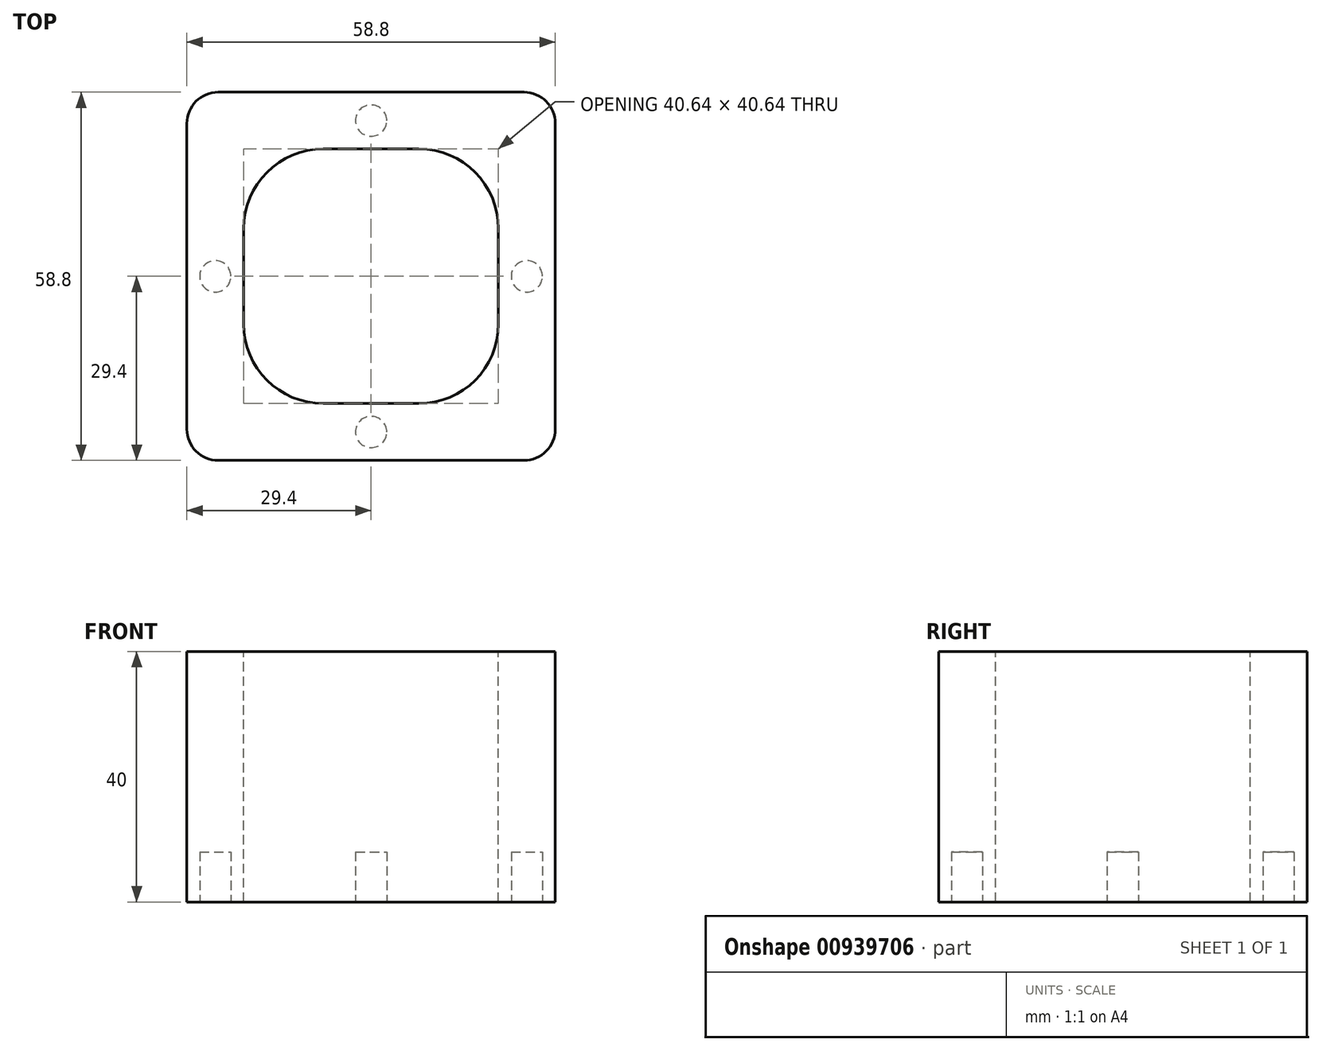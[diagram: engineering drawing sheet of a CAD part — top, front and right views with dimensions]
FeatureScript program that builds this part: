
annotation { "Feature Type Name" : "Feature", "Feature Type Description" : "" }
export const myFeature = defineFeature(function(context is Context, id is Id, definition is map)
    precondition{}
    {
        {
            var Q0;
            Q0=qCreatedBy(makeId("Top.planeOp"),FACE);
            var sketch = newSketch(context, id + "F0", { "sketchPlane" : qUnion([Q0])});
            skLineSegment(sketch, "E0.bottom", {"start": v(29.4, -29.4) * mm, "end": v(-29.4, -29.4) * mm});
            skLineSegment(sketch, "E0.top", {"start": v(29.4, 29.4) * mm, "end": v(-29.4, 29.4) * mm});
            skLineSegment(sketch, "E0.left", {"start": v(29.4, -29.4) * mm, "end": v(29.4, 29.4) * mm});
            skLineSegment(sketch, "E0.right", {"start": v(-29.4, -29.4) * mm, "end": v(-29.4, 29.4) * mm});
            skPoint(sketch, "E0.middle", {"position": v(0, 0) * mm});
            skSolve(sketch);
        }
        {
            var Q0;
            Q0=makeQuery(id+"F0.imprint","IMPRINT",FACE,{"disambiguationData":[TD([[makeQuery(id+"F0.imprint","IMPRINT",EDGE,{"derivedFrom":sQuery(id+"F0.wireOp",EDGE,"E0.bottom")}),-1.0]])]});
            extrude(context, id + "F1", {"entities" : qUnion([Q0]), "depth" : 40 * mm, "offsetDistance" : 25 * mm});
        }
        {
            var Q0;
            Q0=makeQuery(id+"F1.opExtrude","CAP_FACE",FACE,{"disambiguationData":[OSD([sQuery(id+"F0.wireOp",EDGE,"E0.bottom"),sQuery(id+"F0.wireOp",EDGE,"E0.top"),sQuery(id+"F0.wireOp",EDGE,"E0.left"),sQuery(id+"F0.wireOp",EDGE,"E0.right")])],"isStart":false});
            var sketch = newSketch(context, id + "F2", { "sketchPlane" : qUnion([Q0])});
            skLineSegment(sketch, "E1.bottom", {"start": v(20.32, -20.32) * mm, "end": v(-20.32, -20.32) * mm});
            skLineSegment(sketch, "E1.top", {"start": v(20.32, 20.32) * mm, "end": v(-20.32, 20.32) * mm});
            skLineSegment(sketch, "E1.left", {"start": v(20.32, -20.32) * mm, "end": v(20.32, 20.32) * mm});
            skLineSegment(sketch, "E1.right", {"start": v(-20.32, -20.32) * mm, "end": v(-20.32, 20.32) * mm});
            skPoint(sketch, "E1.middle", {"position": v(0, 0) * mm});
            skSolve(sketch);
        }
        {
            var Q0;
            Q0=makeQuery(id+"F2.imprint","IMPRINT",FACE,{"disambiguationData":[TD([[makeQuery(id+"F2.imprint","IMPRINT",EDGE,{"derivedFrom":sQuery(id+"F2.wireOp",EDGE,"E1.bottom")}),-1.0]])]});
            extrude(context, id + "F3", {"entities" : qUnion([Q0]), "operationType" : NewBodyOperationType.REMOVE, "endBound" : BoundingType.THROUGH_ALL, "oppositeDirection" : true, "depth" : 25 * mm, "offsetDistance" : 25 * mm});
        }
        {
            var Q0;
            Q0=makeQuery(id+"F1.opExtrude","CAP_FACE",FACE,{"disambiguationData":[OSD([sQuery(id+"F0.wireOp",EDGE,"E0.bottom"),sQuery(id+"F0.wireOp",EDGE,"E0.top"),sQuery(id+"F0.wireOp",EDGE,"E0.left"),sQuery(id+"F0.wireOp",EDGE,"E0.right")])],"isStart":true});
            var sketch = newSketch(context, id + "F4", { "sketchPlane" : qUnion([Q0])});
            skCircle(sketch, "E2", {"center": v(-24.86, 0) * mm, "radius": 2.5 * mm});
            skCircle(sketch, "E3", {"center": v(0, 24.86) * mm, "radius": 2.5 * mm});
            skCircle(sketch, "E4", {"center": v(24.86, 0) * mm, "radius": 2.5 * mm});
            skCircle(sketch, "E5", {"center": v(0, -24.86) * mm, "radius": 2.5 * mm});
            skSolve(sketch);
        }
        {
            var Q0;
            Q0 = qSketchRegion(id + "F4", true);
            extrude(context, id + "F5", {"entities" : qUnion([Q0]), "operationType" : NewBodyOperationType.REMOVE, "oppositeDirection" : true, "depth" : 8 * mm, "offsetDistance" : 25 * mm});
        }
        {
            var Q0;
            Q0=makeQuery(id+"F3.boolean.opBoolean","COPY",EDGE,{"derivedFrom":makeQuery(id+"F3.opExtrude","SWEPT_EDGE",EDGE,{"disambiguationData":[OSD([sQuery(id+"F2.wireOp",EDGE,"E1.top"),sQuery(id+"F2.wireOp",EDGE,"E1.right")])]})});
            var Q1;
            Q1=makeQuery(id+"F3.boolean.opBoolean","COPY",EDGE,{"derivedFrom":makeQuery(id+"F3.opExtrude","SWEPT_EDGE",EDGE,{"disambiguationData":[OSD([sQuery(id+"F2.wireOp",EDGE,"E1.top"),sQuery(id+"F2.wireOp",EDGE,"E1.left")])]})});
            var Q2;
            Q2=makeQuery(id+"F3.boolean.opBoolean","COPY",EDGE,{"derivedFrom":makeQuery(id+"F3.opExtrude","SWEPT_EDGE",EDGE,{"disambiguationData":[OSD([sQuery(id+"F2.wireOp",EDGE,"E1.bottom"),sQuery(id+"F2.wireOp",EDGE,"E1.left")])]})});
            var Q3;
            Q3=makeQuery(id+"F3.boolean.opBoolean","COPY",EDGE,{"derivedFrom":makeQuery(id+"F3.opExtrude","SWEPT_EDGE",EDGE,{"disambiguationData":[OSD([sQuery(id+"F2.wireOp",EDGE,"E1.bottom"),sQuery(id+"F2.wireOp",EDGE,"E1.right")])]})});
            fillet(context, id + "F6", {"entities" : qUnion([Q0, Q1, Q2, Q3]), "radius" : 12.7 * mm, "tangentPropagation" : true, "allowEdgeOverflow" : false});
        }
        {
            var Q0;
            Q0=makeQuery(id+"F1.opExtrude","SWEPT_EDGE",EDGE,{"disambiguationData":[OSD([sQuery(id+"F0.wireOp",EDGE,"E0.bottom"),sQuery(id+"F0.wireOp",EDGE,"E0.right")])]});
            var Q1;
            Q1=makeQuery(id+"F1.opExtrude","SWEPT_EDGE",EDGE,{"disambiguationData":[OSD([sQuery(id+"F0.wireOp",EDGE,"E0.top"),sQuery(id+"F0.wireOp",EDGE,"E0.right")])]});
            var Q2;
            Q2=makeQuery(id+"F1.opExtrude","SWEPT_EDGE",EDGE,{"disambiguationData":[OSD([sQuery(id+"F0.wireOp",EDGE,"E0.bottom"),sQuery(id+"F0.wireOp",EDGE,"E0.left")])]});
            var Q3;
            Q3=makeQuery(id+"F1.opExtrude","SWEPT_EDGE",EDGE,{"disambiguationData":[OSD([sQuery(id+"F0.wireOp",EDGE,"E0.top"),sQuery(id+"F0.wireOp",EDGE,"E0.left")])]});
            fillet(context, id + "F7", {"entities" : qUnion([Q0, Q1, Q2, Q3]), "radius" : 5 * mm, "tangentPropagation" : true, "allowEdgeOverflow" : false});
        }
    });
